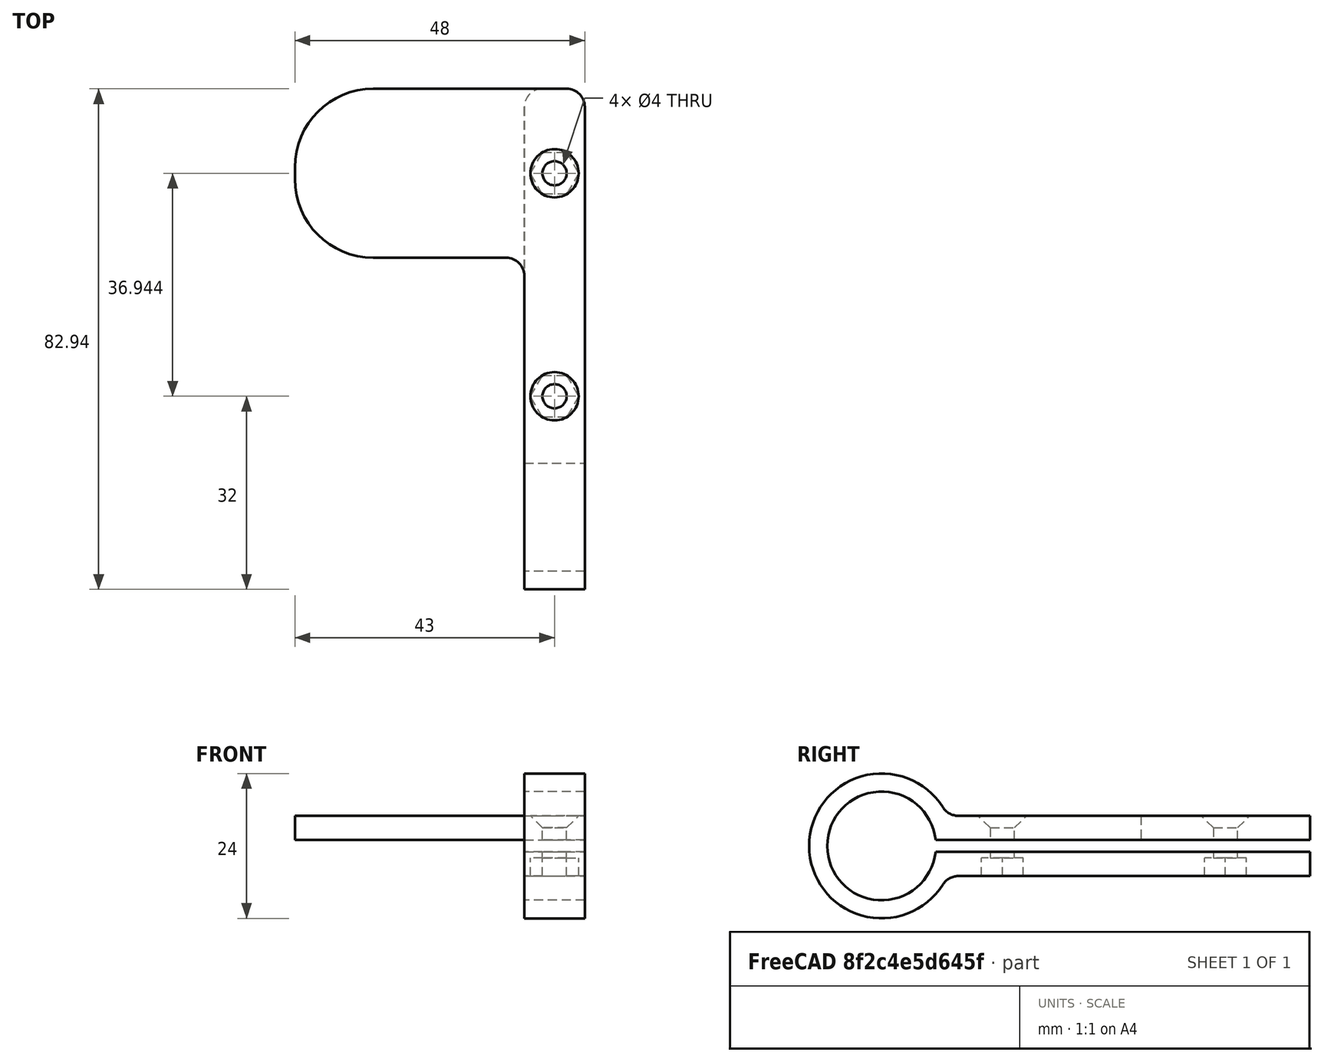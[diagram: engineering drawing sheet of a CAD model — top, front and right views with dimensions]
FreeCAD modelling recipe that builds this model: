
FCSTD DOCUMENT  (FreeCAD 0.17R13522 (Git))
Label: supportTelepeage18mm
License: All rights reserved
LicenseURL: http://en.wikipedia.org/wiki/All_rights_reserved
objects: PartDesign::Fillet×5, Sketcher::SketchObject×4, PartDesign::Pad×2, PartDesign::Pocket×2, PartDesign::Chamfer×1, PartDesign::Body×1, Mesh::Feature×1
note: 19 computed .brp shape members not serialized (recipe doc carries the construction recipe); baked Part::Feature solids carry a one-line shape summary decoded from their .brp

FEATURE [Sketcher::SketchObject] Sketch
  MapMode = 5
  Placement = pos=(0,0,0) rot=(0.57735,0.57735,0.57735;2.0944rad)
  Support = -> [YZ_Plane]
  sketch-geometry (8):
    g0: ArcOfCircle CenterX=0 CenterY=0 CenterZ=0 NormalX=0 NormalY=0 NormalZ=1 AngleXU=0 Radius=9 StartAngle=0.111341 EndAngle=6.17184
    g1: ArcOfCircle CenterX=0 CenterY=0 CenterZ=0 NormalX=0 NormalY=0 NormalZ=1 AngleXU=0 Radius=12 StartAngle=0.429775 EndAngle=5.85341
    g2: LineSegment StartX=8.94427 StartY=1 StartZ=0 EndX=70.9443 EndY=1 EndZ=0
    g3: LineSegment StartX=70.9443 StartY=1 StartZ=0 EndX=70.9443 EndY=5 EndZ=0
    g4: LineSegment StartX=70.9443 StartY=5 StartZ=0 EndX=10.9087 EndY=5 EndZ=0
    g5: LineSegment StartX=8.94427 StartY=-1 StartZ=0 EndX=70.9443 EndY=-1 EndZ=0
    g6: LineSegment StartX=70.9443 StartY=-1 StartZ=0 EndX=70.9443 EndY=-5 EndZ=0
    g7: LineSegment StartX=70.9443 StartY=-5 StartZ=0 EndX=10.9087 EndY=-5 EndZ=0
  constraints (24):
    c: Radius(g0) = 9
    c: Coincident(g0,g-1)
    c: DistanceY(g-1,g0) = -1
    c: DistanceY(g-1,g0) = 1
    c: Radius(g1) = 12
    c: Coincident(g1,g-1)
    c: DistanceY(g-1,g1) = 5
    c: DistanceY(g1,g-1) = 5
    c: Horizontal(g2)
    c: Coincident(g2,g3)
    c: Vertical(g3)
    c: Coincident(g3,g4)
    c: Horizontal(g4)
    c: Coincident(g4,g1)
    c: Coincident(g2,g0)
    c: DistanceX(g2,g2) = 62
    c: Horizontal(g5)
    c: Coincident(g5,g6)
    c: Coincident(g6,g7)
    c: Horizontal(g7)
    c: Vertical(g6)
    c: Symmetric(g2,g5,g-1)
    c: Coincident(g5,g0)
    c: Coincident(g7,g1)
FEATURE [PartDesign::Pad] Pad
  Length = 10
  Length2 = 100
  Placement = pos=(0,0,0) rot=(0.57735,0.57735,0.57735;2.0944rad)
  Profile = -> Sketch
  Type = 0
FEATURE [Sketcher::SketchObject] Sketch001
  ExternalGeometry = -> [Pad]
  MapMode = 5
  Placement = pos=(0,0,0) rot=(0.57735,0.57735,-0.57735;4.18879rad)
  Support = -> [Pad]
  sketch-geometry (4):
    g0: LineSegment StartX=42.9443 StartY=-1 StartZ=0 EndX=70.9443 EndY=-1 EndZ=0
    g1: LineSegment StartX=70.9443 StartY=-1 StartZ=0 EndX=70.9443 EndY=-5 EndZ=0
    g2: LineSegment StartX=70.9443 StartY=-5 StartZ=0 EndX=42.9443 EndY=-5 EndZ=0
    g3: LineSegment StartX=42.9443 StartY=-5 StartZ=0 EndX=42.9443 EndY=-1 EndZ=0
  constraints (11):
    c: Coincident(g0,g1)
    c: Coincident(g1,g2)
    c: Coincident(g2,g3)
    c: Coincident(g3,g0)
    c: Horizontal(g0)
    c: Horizontal(g2)
    c: Vertical(g1)
    c: Vertical(g3)
    c: Coincident(g0,g-3)
    c: Coincident(g1,g-4)
    c: DistanceX(g2,g2) = 28
FEATURE [PartDesign::Pad] Pad001
  BaseFeature = -> Pad
  Length = 38
  Length2 = 100
  Placement = pos=(0,0,0) rot=(0.57735,0.57735,0.57735;2.0944rad)
  Profile = -> Sketch001
  Type = 0
FEATURE [PartDesign::Fillet] Fillet
  Base = -> Pad001 [Edge29,Edge33]
  BaseFeature = -> Pad001
  Placement = pos=(0,0,0) rot=(0.57735,0.57735,0.57735;2.0944rad)
  Radius = 13
FEATURE [Sketcher::SketchObject] Sketch002
  ExternalGeometry = -> [Fillet]
  MapMode = 5
  Placement = pos=(1e-12,-1e-12,-5) rot=(0.707107,0.707107,0;3.14159rad)
  Support = -> [Fillet]
  sketch-geometry (14):
    g0: LineSegment StartX=23.4641 StartY=3 StartZ=0 EndX=23.4641 EndY=7 EndZ=0
    g1: LineSegment StartX=23.4641 StartY=7 StartZ=0 EndX=20 EndY=9 EndZ=0
    g2: LineSegment StartX=20 StartY=9 StartZ=0 EndX=16.5359 EndY=7 EndZ=0
    g3: LineSegment StartX=16.5359 StartY=7 StartZ=0 EndX=16.5359 EndY=3 EndZ=0
    g4: LineSegment StartX=16.5359 StartY=3 StartZ=0 EndX=20 EndY=1 EndZ=0
    g5: LineSegment StartX=20 StartY=1 StartZ=0 EndX=23.4641 EndY=3 EndZ=0
    g6: Circle [constr] CenterX=20 CenterY=5 CenterZ=0 NormalX=0 NormalY=0 NormalZ=1 AngleXU=0 Radius=4
    g7: LineSegment StartX=60.4084 StartY=3 StartZ=0 EndX=60.4084 EndY=7 EndZ=0
    g8: LineSegment StartX=60.4084 StartY=7 StartZ=0 EndX=56.9443 EndY=9 EndZ=0
    g9: LineSegment StartX=56.9443 StartY=9 StartZ=0 EndX=53.4802 EndY=7 EndZ=0
    g10: LineSegment StartX=53.4802 StartY=7 StartZ=0 EndX=53.4802 EndY=3 EndZ=0
    g11: LineSegment StartX=53.4802 StartY=3 StartZ=0 EndX=56.9443 EndY=1 EndZ=0
    g12: LineSegment StartX=56.9443 StartY=1 StartZ=0 EndX=60.4084 EndY=3 EndZ=0
    g13: Circle [constr] CenterX=56.9443 CenterY=5 CenterZ=0 NormalX=0 NormalY=0 NormalZ=1 AngleXU=0 Radius=4
  constraints (34):
    c: Coincident(g0,g1)
    c: Coincident(g1,g2)
    c: Coincident(g2,g3)
    c: Coincident(g3,g4)
    c: Coincident(g4,g5)
    c: Coincident(g5,g0)
    c: Equal(g0, g1-g5) x5
    c: PointOnObject(g0,g6)
    c: PointOnObject(g1,g6)
    c: PointOnObject(g2,g6)
    c: PointOnObject(g3,g6)
    c: PointOnObject(g4,g6)
    c: PointOnObject(g5,g6)
    c: Radius(g6) = 4
    c: Vertical(g3)
    c: DistanceX(g-1,g6) = 20
    c: DistanceY(g-1,g6) = 5
    c: Coincident(g7,g8)
    c: Coincident(g8,g9)
    c: Coincident(g9,g10)
    c: Coincident(g10,g11)
    c: Coincident(g11,g12)
    c: Coincident(g12,g7)
    c: Equal(g7, g8-g12) x5
    c: PointOnObject(g7,g13)
    c: PointOnObject(g8,g13)
    c: PointOnObject(g9,g13)
    c: PointOnObject(g10,g13)
    c: PointOnObject(g11,g13)
    c: PointOnObject(g12,g13)
    c: Equal(g6,g13) = 4
    c: Vertical(g10)
    c: DistanceY(g-1,g13) = 5
    c: DistanceX(g13,g-3) = 14
FEATURE [PartDesign::Pocket] Pocket
  BaseFeature = -> Fillet
  Length = 3
  Length2 = 100
  Placement = pos=(0,0,0) rot=(0.57735,0.57735,0.57735;2.0944rad)
  Profile = -> Sketch002
  Type = 0
FEATURE [Sketcher::SketchObject] Sketch003
  ExternalGeometry = -> [Pocket]
  MapMode = 5
  Placement = pos=(-1e-12,1e-12,5) rot=(0,0,-1;1.5708rad)
  Support = -> [Pocket]
  sketch-geometry (2):
    g0: Circle CenterX=-20 CenterY=5 CenterZ=0 NormalX=0 NormalY=0 NormalZ=1 AngleXU=0 Radius=2
    g1: Circle CenterX=-56.9443 CenterY=5 CenterZ=0 NormalX=0 NormalY=0 NormalZ=1 AngleXU=0 Radius=2
  constraints (6):
    c: Radius(g0) = 2
    c: DistanceX(g0,g-1) = 20
    c: DistanceY(g-1,g0) = 5
    c: Equal(g0,g1) = 2
    c: DistanceY(g-1,g1) = 5
    c: DistanceX(g-3,g1) = 14
FEATURE [PartDesign::Pocket] Pocket001
  BaseFeature = -> Pocket
  Length = 7
  Length2 = 100
  Placement = pos=(0,0,0) rot=(0.57735,0.57735,0.57735;2.0944rad)
  Profile = -> Sketch003
  Type = 0
FEATURE [PartDesign::Chamfer] Chamfer
  Base = -> Pocket001 [Edge42,Edge40]
  BaseFeature = -> Pocket001
  Placement = pos=(0,0,0) rot=(0.57735,0.57735,0.57735;2.0944rad)
  Size = 2
FEATURE [PartDesign::Fillet] Fillet001
  Base = -> Chamfer [Edge17]
  BaseFeature = -> Chamfer
  Placement = pos=(0,0,0) rot=(0.57735,0.57735,0.57735;2.0944rad)
  Radius = 3
FEATURE [PartDesign::Fillet] Fillet002
  Base = -> Fillet001 [Edge36]
  BaseFeature = -> Fillet001
  Placement = pos=(0,0,0) rot=(0.57735,0.57735,0.57735;2.0944rad)
  Radius = 3
FEATURE [PartDesign::Fillet] Fillet003
  Base = -> Fillet002 [Edge38,Edge6,Edge7]
  BaseFeature = -> Fillet002
  Placement = pos=(0,0,0) rot=(0.57735,0.57735,0.57735;2.0944rad)
  Radius = 3
FEATURE [PartDesign::Fillet] Fillet004
  Base = -> Fillet003 [Edge58]
  BaseFeature = -> Fillet003
  Placement = pos=(0,0,0) rot=(0.57735,0.57735,0.57735;2.0944rad)
  Radius = 3
FEATURE [PartDesign::Body] Body
  Group = -> [Sketch,Pad,Sketch001,Pad001,Fillet,Sketch002,Pocket,Sketch003,Pocket001,Chamfer,Fillet001,Fillet002,Fillet003,Fillet004]
  Origin = -> Origin
  Tip = -> Fillet004
FEATURE [Mesh::Feature] Mesh  label="Body (Meshed)"
